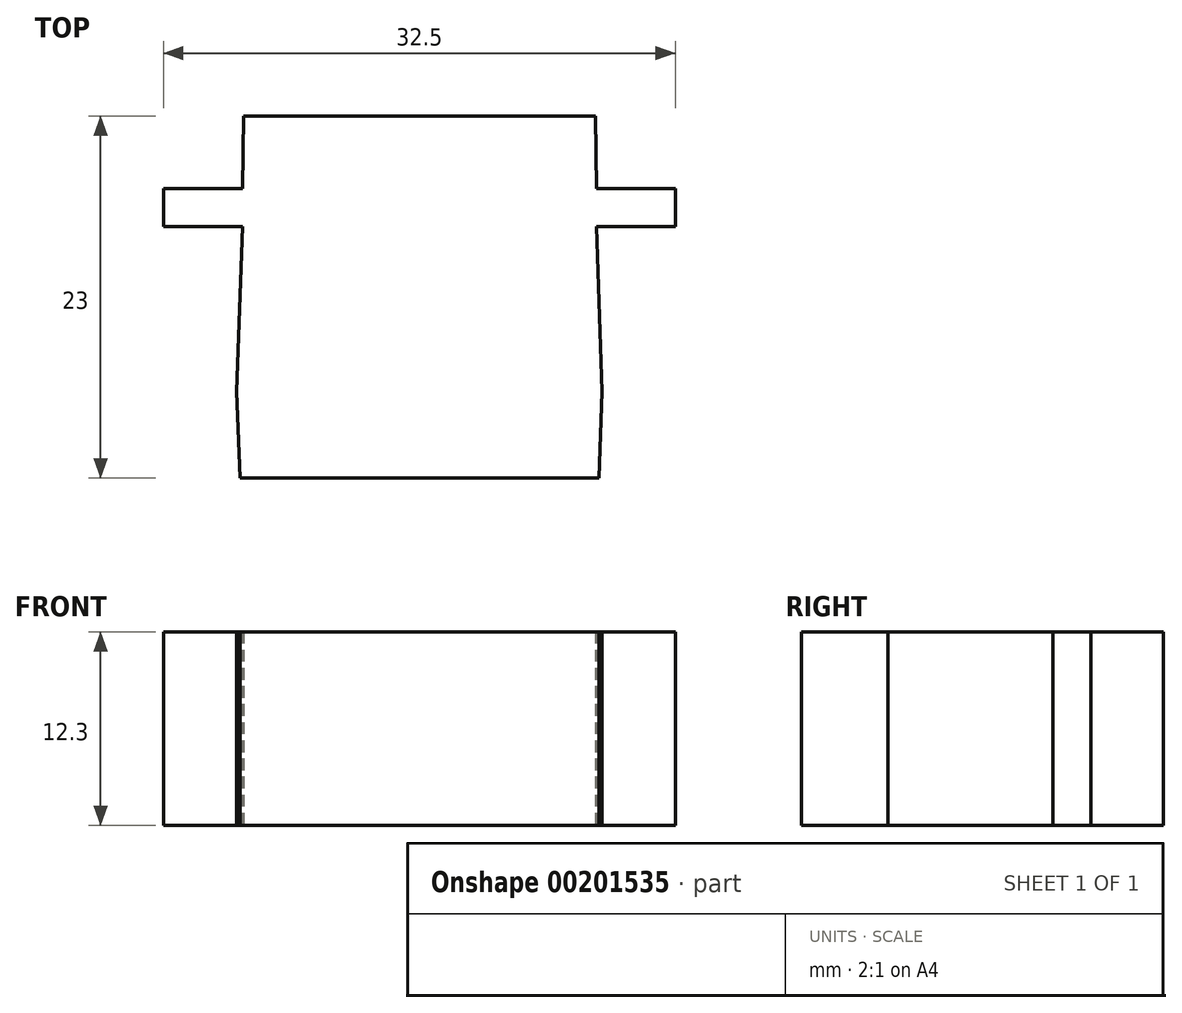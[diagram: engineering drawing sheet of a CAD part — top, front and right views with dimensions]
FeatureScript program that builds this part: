
annotation { "Feature Type Name" : "Feature", "Feature Type Description" : "" }
export const myFeature = defineFeature(function(context is Context, id is Id, definition is map)
    precondition{}
    {
        {
            var Q0;
            Q0=qCreatedBy(makeId("Top.planeOp"),FACE);
            var sketch = newSketch(context, id + "F0", { "sketchPlane" : qUnion([Q0])});
            skLineSegment(sketch, "E0", {"start": v(-16.25, 10.5) * mm, "end": v(16.25, 10.5) * mm, "construction": true});
            skLineSegment(sketch, "E1", {"start": v(-16.25, 10.5) * mm, "end": v(-11.25, 10.5) * mm});
            skLineSegment(sketch, "E2", {"start": v(-11.25, 10.5) * mm, "end": v(-11.6, 0) * mm});
            skLineSegment(sketch, "E3", {"start": v(-11.6, 0) * mm, "end": v(11.6, 0) * mm, "construction": true});
            skLineSegment(sketch, "E4", {"start": v(0, 10.5) * mm, "end": v(0, 0) * mm, "construction": true});
            skLineSegment(sketch, "E5.MirrorCS", {"start": v(11.25, 10.5) * mm, "end": v(11.6, 0) * mm});
            skLineSegment(sketch, "E6.MirrorCS", {"start": v(16.25, 10.5) * mm, "end": v(11.25, 10.5) * mm});
            skLineSegment(sketch, "E7", {"start": v(-11.4, -5.5) * mm, "end": v(11.4, -5.5) * mm});
            skLineSegment(sketch, "E8", {"start": v(0, 0) * mm, "end": v(0, -5.5) * mm, "construction": true});
            skLineSegment(sketch, "E9", {"start": v(11.4, -5.5) * mm, "end": v(11.6, 0) * mm});
            skLineSegment(sketch, "E10", {"start": v(-11.4, -5.5) * mm, "end": v(-11.6, 0) * mm});
            skLineSegment(sketch, "E11", {"start": v(-16.25, 10.5) * mm, "end": v(-16.25, 12.9) * mm});
            skLineSegment(sketch, "E12", {"start": v(-16.25, 12.9) * mm, "end": v(-11.25, 12.9) * mm});
            skLineSegment(sketch, "E13", {"start": v(0, 10.5) * mm, "end": v(0, 17.5) * mm, "construction": true});
            skLineSegment(sketch, "E14", {"start": v(-11.18, 17.5) * mm, "end": v(11.18, 17.5) * mm});
            skLineSegment(sketch, "E15", {"start": v(-11.25, 12.9) * mm, "end": v(-11.17, 17.5) * mm});
            skLineSegment(sketch, "E16.MirrorCS", {"start": v(11.25, 12.9) * mm, "end": v(11.17, 17.5) * mm});
            skLineSegment(sketch, "E17.MirrorCS", {"start": v(16.25, 12.9) * mm, "end": v(11.25, 12.9) * mm});
            skLineSegment(sketch, "E18.MirrorCS", {"start": v(16.25, 10.5) * mm, "end": v(16.25, 12.9) * mm});
            skSolve(sketch);
        }
        {
            var Q0;
            Q0=makeQuery(id+"F0.imprint","IMPRINT",FACE,{"disambiguationData":[TD([[makeQuery(id+"F0.imprint","IMPRINT",EDGE,{"derivedFrom":sQuery(id+"F0.wireOp",EDGE,"E1")}),1.0]])]});
            extrude(context, id + "F1", {"entities" : qUnion([Q0]), "endBound" : BoundingType.SYMMETRIC, "depth" : 12.3 * mm});
        }
    });
